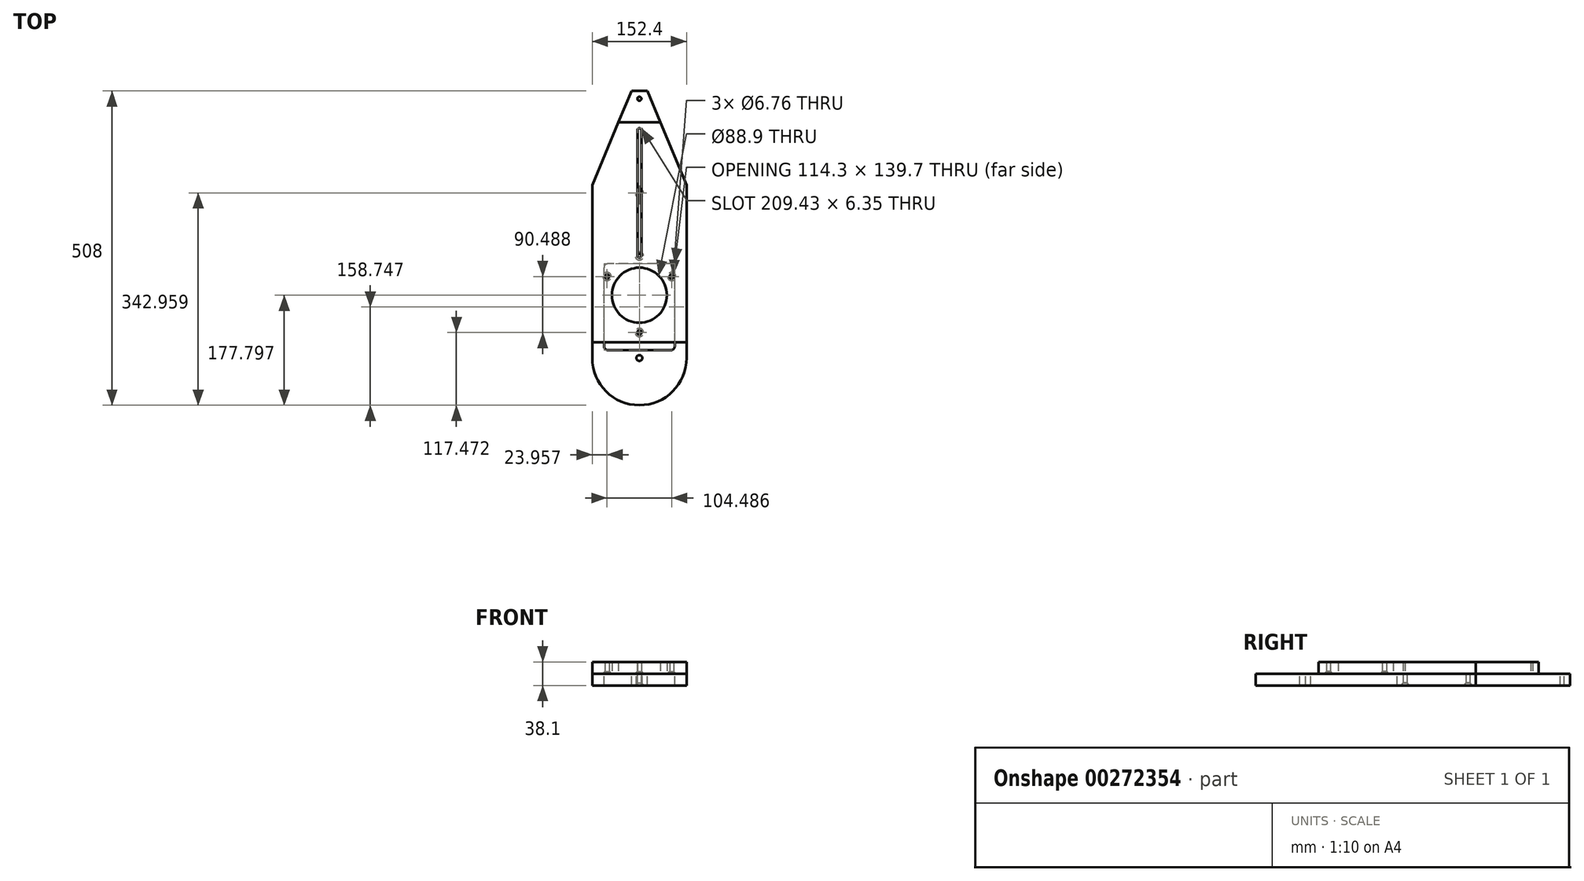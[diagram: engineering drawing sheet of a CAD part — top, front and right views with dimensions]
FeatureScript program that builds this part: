
annotation { "Feature Type Name" : "Feature", "Feature Type Description" : "" }
export const myFeature = defineFeature(function(context is Context, id is Id, definition is map)
    precondition{}
    {
        {
            var Q0;
            Q0=qCreatedBy(makeId("Top.planeOp"),FACE);
            var sketch = newSketch(context, id + "F0", { "sketchPlane" : qUnion([Q0])});
            skLineSegment(sketch, "E0.bottom", {"start": v(-112.58, 63.43) * mm, "end": v(-44.84, 63.43) * mm});
            skLineSegment(sketch, "E0.top", {"start": v(-154.9, -292.17) * mm, "end": v(-2.5, -292.17) * mm});
            skLineSegment(sketch, "E0.left", {"start": v(-154.9, -38.17) * mm, "end": v(-154.9, -292.17) * mm});
            skLineSegment(sketch, "E0.right", {"start": v(-2.5, -38.17) * mm, "end": v(-2.5, -292.17) * mm});
            skCircle(sketch, "E1", {"center": v(-78.7, -215.97) * mm, "radius": 44.45 * mm});
            skPoint(sketch, "E1.centerSnap0", {"position": v(-78.7, -292.17) * mm});
            skPoint(sketch, "E2", {"position": v(-78.7, -276.3) * mm});
            skLineSegment(sketch, "E3", {"start": v(-78.7, -215.97) * mm, "end": v(-0.55, -170.85) * mm, "construction": true});
            skLineSegment(sketch, "E4", {"start": v(-78.7, -215.97) * mm, "end": v(-157.21, -170.65) * mm, "construction": true});
            skCircle(sketch, "E5", {"center": v(-78.7, -215.97) * mm, "radius": 60.33 * mm, "construction": true});
            skPoint(sketch, "E6", {"position": v(-26.47, -185.81) * mm});
            skPoint(sketch, "E7", {"position": v(-130.95, -185.81) * mm});
            skLineSegment(sketch, "E8", {"start": v(-78.7, -165.17) * mm, "end": v(-78.7, 11.88) * mm, "construction": true});
            skLineSegment(sketch, "E9.left", {"start": v(-75.54, 50.85) * mm, "end": v(-75.53, -152.35) * mm});
            skLineSegment(sketch, "E9.right", {"start": v(-81.89, 50.73) * mm, "end": v(-81.88, -152.47) * mm});
            skPoint(sketch, "E9.middle", {"position": v(-78.7, -50.81) * mm});
            skArc(sketch, "E10", {"start": v(-81.89, 50.73) * mm, "mid": v(-78.77, 53.9) * mm, "end": v(-75.54, 50.85) * mm});
            skArc(sketch, "E11", {"start": v(-75.53, -152.35) * mm, "mid": v(-78.65, -155.52) * mm, "end": v(-81.88, -152.47) * mm});
            skCircle(sketch, "E12", {"center": v(-78.7, -317.57) * mm, "radius": 4.76 * mm});
            skLineSegment(sketch, "E13.bottom", {"start": v(-2.5, -292.17) * mm, "end": v(-154.9, -292.17) * mm});
            skLineSegment(sketch, "E13.left", {"start": v(-2.5, -292.17) * mm, "end": v(-2.5, -317.57) * mm});
            skLineSegment(sketch, "E13.right", {"start": v(-154.9, -292.17) * mm, "end": v(-154.9, -317.57) * mm});
            skLineSegment(sketch, "E14", {"start": v(-2.5, -38.17) * mm, "end": v(-66, 114.23) * mm});
            skLineSegment(sketch, "E15", {"start": v(-66, 114.23) * mm, "end": v(-78.7, 114.23) * mm});
            skLineSegment(sketch, "E16.MirrorCS", {"start": v(-154.9, -38.17) * mm, "end": v(-91.4, 114.23) * mm});
            skLineSegment(sketch, "E17.MirrorCS", {"start": v(-91.4, 114.23) * mm, "end": v(-78.7, 114.23) * mm});
            skCircle(sketch, "E18", {"center": v(-78.7, 101.53) * mm, "radius": 3.18 * mm});
            skLineSegment(sketch, "E19.bottom", {"start": v(-78.7, -304.87) * mm, "end": v(-27.9, -304.87) * mm});
            skLineSegment(sketch, "E19.top", {"start": v(-78.7, -165.17) * mm, "end": v(-27.9, -165.17) * mm});
            skLineSegment(sketch, "E19.right", {"start": v(-21.56, -298.52) * mm, "end": v(-21.56, -171.52) * mm});
            skLineSegment(sketch, "E20.trimOffspring", {"start": v(-78.7, -304.87) * mm, "end": v(-78.7, -314.95) * mm, "construction": true});
            skPoint(sketch, "E21.visualSharp", {"position": v(-21.56, -165.17) * mm});
            skArc(sketch, "E21.filletArc", {"start": v(-21.56, -171.52) * mm, "mid": v(-23.42, -167.03) * mm, "end": v(-27.9, -165.17) * mm});
            skPoint(sketch, "E22.visualSharp", {"position": v(-21.56, -304.87) * mm});
            skArc(sketch, "E22.filletArc", {"start": v(-27.9, -304.87) * mm, "mid": v(-23.42, -303.01) * mm, "end": v(-21.56, -298.52) * mm});
            skLineSegment(sketch, "E23.MirrorCS", {"start": v(-78.7, -165.17) * mm, "end": v(-129.5, -165.17) * mm});
            skArc(sketch, "E24.MirrorCS", {"start": v(-135.86, -171.52) * mm, "mid": v(-134, -167.03) * mm, "end": v(-129.5, -165.17) * mm});
            skLineSegment(sketch, "E25.MirrorCS", {"start": v(-135.86, -298.52) * mm, "end": v(-135.86, -171.52) * mm});
            skArc(sketch, "E26.MirrorCS", {"start": v(-129.5, -304.87) * mm, "mid": v(-134, -303.01) * mm, "end": v(-135.86, -298.52) * mm});
            skLineSegment(sketch, "E27.MirrorCS", {"start": v(-78.7, -304.87) * mm, "end": v(-129.5, -304.87) * mm});
            skArc(sketch, "E28", {"start": v(-81.88, -152.47) * mm, "mid": v(-78.65, -155.52) * mm, "end": v(-75.53, -152.35) * mm});
            skArc(sketch, "E29", {"start": v(-154.9, -317.57) * mm, "mid": v(-78.7, -393.77) * mm, "end": v(-2.5, -317.57) * mm});
            skPoint(sketch, "E30.center.orphan", {"position": v(-78.7, -50.87) * mm});
            skSolve(sketch);
        }
        {
            var Q0;
            {var subQ8=sQuery(id+"F0.wireOp",EDGE,"E0.bottom");Q0=makeQuery(id+"F0.imprint","IMPRINT",FACE,{"disambiguationData":[TD([[makeQuery(id+"F0.imprint","IMPRINT",EDGE,{"derivedFrom":subQ8}),-1.0]])]});}
            var Q1;
            Q1=makeQuery(id+"F0.imprint","IMPRINT",FACE,{"disambiguationData":[TD([[makeQuery(id+"F0.imprint","IMPRINT",EDGE,{"derivedFrom":sQuery(id+"F0.wireOp",EDGE,"E1")}),-1.0]])]});
            extrude(context, id + "F1", {"entities" : qUnion([Q0, Q1]), "depth" : 19.05 * mm});
        }
        {
            var Q0;
            Q0=sQuery(id+"F0.wireOp",VERTEX,"E6");
            var Q1;
            Q1=sQuery(id+"F0.wireOp",VERTEX,"E7");
            var Q2;
            Q2=sQuery(id+"F0.wireOp",VERTEX,"E2");
            var Q3;
            Q3=makeQuery(id+"F1.opExtrude","SWEPT_BODY",BODY,{"disambiguationData":[OSD([sQuery(id+"F0.wireOp",EDGE,"E0.bottom"),sQuery(id+"F0.wireOp",EDGE,"E0.top"),sQuery(id+"F0.wireOp",EDGE,"E0.left"),sQuery(id+"F0.wireOp",EDGE,"E0.right"),sQuery(id+"F0.wireOp",EDGE,"E1")])]});
            hole(context, id + "F2", {"style" : HoleStyle.C_SINK, "endStyle" : HoleEndStyle.THROUGH, "oppositeDirection" : true, "standardTappedOrClearance" : lookupTablePath({ "standard" : "ANSI", "fit" : "Normal (ASME)", "size" : "1/4", "type" : "Clearance" }), "standardBlindInLast" : lookupTablePath({ "fit" : "Free", "standard" : "ANSI", "size" : "1/4", "type" : "Clearance" }), "holeDiameter" : 6.76 * mm, "cSinkDiameter" : 13.5 * mm, "cSinkAngle" : 82 * degree, "isTappedThrough" : true, "tappedDepth" : 15.56 * mm, "tapClearance" : 3, "startFromSketch" : true, "locations" : qUnion([Q0, Q1, Q2]), "scope" : qUnion([Q3])});
        }
        {
            var Q0;
            Q0=makeQuery(id+"F0.imprint","IMPRINT",FACE,{"disambiguationData":[TD([[makeQuery(id+"F0.imprint","IMPRINT",EDGE,{"derivedFrom":sQuery(id+"F0.wireOp",EDGE,"E12")}),-1.0]])]});
            var Q1;
            {var subQ0=sQuery(id+"F0.wireOp",EDGE,"E0.bottom");Q1=makeQuery(id+"F0.imprint","IMPRINT",FACE,{"disambiguationData":[TD([[makeQuery(id+"F0.imprint","IMPRINT",EDGE,{"derivedFrom":subQ0}),-1.0]])]});}
            var Q2;
            {var subQ1=sQuery(id+"F0.wireOp",EDGE,"E0.bottom");Q2=makeQuery(id+"F0.imprint","IMPRINT",FACE,{"disambiguationData":[TD([[makeQuery(id+"F0.imprint","IMPRINT",EDGE,{"derivedFrom":subQ1}),1.0]])]});}
            var Q3;
            {var subQ0=sQuery(id+"F0.wireOp",EDGE,"E28");var subQ1=sQuery(id+"F0.wireOp",EDGE,"E9.left");var subQ2=makeQuery(id+"F0.imprint","INTERSECT",VERTEX,{"derivedFrom":[subQ1,subQ0]});Q3=makeQuery(id+"F0.imprint","IMPRINT",FACE,{"disambiguationData":[TD([[makeQuery(id+"F0.imprint","IMPRINT",EDGE,{"disambiguationData":[TD([[subQ2,1.0]])],"derivedFrom":subQ1}),-1.0]])]});}
            var Q4;
            {var subQ0=sQuery(id+"F0.wireOp",EDGE,"E10");Q4=makeQuery(id+"F0.imprint","IMPRINT",FACE,{"disambiguationData":[TD([[makeQuery(id+"F0.imprint","IMPRINT",EDGE,{"derivedFrom":subQ0}),-1.0]])]});}
            extrude(context, id + "F3", {"entities" : qUnion([Q0, Q1, Q2, Q3, Q4]), "oppositeDirection" : true, "depth" : 19.05 * mm});
        }
        {
            var Q0;
            Q0=makeQuery(id+"F3.opExtrude","CAP_FACE",FACE,{"disambiguationData":[OSD([sQuery(id+"F0.wireOp",EDGE,"E0.left"),sQuery(id+"F0.wireOp",EDGE,"E0.right"),sQuery(id+"F0.wireOp",EDGE,"E12"),sQuery(id+"F0.wireOp",EDGE,"E13.left"),sQuery(id+"F0.wireOp",EDGE,"E13.right"),sQuery(id+"F0.wireOp",EDGE,"E14"),sQuery(id+"F0.wireOp",EDGE,"E15"),sQuery(id+"F0.wireOp",EDGE,"E16.MirrorCS"),sQuery(id+"F0.wireOp",EDGE,"E17.MirrorCS"),sQuery(id+"F0.wireOp",EDGE,"E18"),sQuery(id+"F0.wireOp",EDGE,"E19.bottom"),sQuery(id+"F0.wireOp",EDGE,"E19.top"),sQuery(id+"F0.wireOp",EDGE,"E19.right"),sQuery(id+"F0.wireOp",EDGE,"E21.filletArc"),sQuery(id+"F0.wireOp",EDGE,"E22.filletArc"),sQuery(id+"F0.wireOp",EDGE,"E23.MirrorCS"),sQuery(id+"F0.wireOp",EDGE,"E24.MirrorCS"),sQuery(id+"F0.wireOp",EDGE,"E25.MirrorCS"),sQuery(id+"F0.wireOp",EDGE,"E26.MirrorCS"),sQuery(id+"F0.wireOp",EDGE,"E27.MirrorCS"),sQuery(id+"F0.wireOp",EDGE,"E29")])],"isStart":false});
            var sketch = newSketch(context, id + "F4", { "sketchPlane" : qUnion([Q0])});
            skLineSegment(sketch, "E31.0", {"start": v(-78.7, 165.17) * mm, "end": v(-78.7, -11.88) * mm, "construction": true});
            skPoint(sketch, "E32", {"position": v(-78.7, 152.47) * mm});
            skPoint(sketch, "E33", {"position": v(-78.7, 50.87) * mm});
            skSolve(sketch);
        }
        {
            var Q0;
            Q0=sQuery(id+"F4.wireOp",VERTEX,"E32");
            var Q1;
            Q1=sQuery(id+"F4.wireOp",VERTEX,"E33");
            var Q2;
            Q2=makeQuery(id+"F3.opExtrude","SWEPT_BODY",BODY,{"disambiguationData":[OSD([sQuery(id+"F0.wireOp",EDGE,"E0.left"),sQuery(id+"F0.wireOp",EDGE,"E0.right"),sQuery(id+"F0.wireOp",EDGE,"E12"),sQuery(id+"F0.wireOp",EDGE,"E13.left"),sQuery(id+"F0.wireOp",EDGE,"E13.right"),sQuery(id+"F0.wireOp",EDGE,"E14"),sQuery(id+"F0.wireOp",EDGE,"E15"),sQuery(id+"F0.wireOp",EDGE,"E16.MirrorCS"),sQuery(id+"F0.wireOp",EDGE,"E17.MirrorCS"),sQuery(id+"F0.wireOp",EDGE,"E18"),sQuery(id+"F0.wireOp",EDGE,"E19.bottom"),sQuery(id+"F0.wireOp",EDGE,"E19.top"),sQuery(id+"F0.wireOp",EDGE,"E19.right"),sQuery(id+"F0.wireOp",EDGE,"E21.filletArc"),sQuery(id+"F0.wireOp",EDGE,"E22.filletArc"),sQuery(id+"F0.wireOp",EDGE,"E23.MirrorCS"),sQuery(id+"F0.wireOp",EDGE,"E24.MirrorCS"),sQuery(id+"F0.wireOp",EDGE,"E25.MirrorCS"),sQuery(id+"F0.wireOp",EDGE,"E26.MirrorCS"),sQuery(id+"F0.wireOp",EDGE,"E27.MirrorCS"),sQuery(id+"F0.wireOp",EDGE,"E29")])]});
            hole(context, id + "F5", {"style" : HoleStyle.C_SINK, "endStyle" : HoleEndStyle.THROUGH, "standardTappedOrClearance" : lookupTablePath({ "standard" : "ANSI", "fit" : "Close", "size" : "1/4", "type" : "Clearance" }), "standardBlindInLast" : lookupTablePath({ "fit" : "Close", "standard" : "ANSI", "size" : "1/4", "type" : "Clearance" }), "holeDiameter" : 6.53 * mm, "cSinkDiameter" : 13.5 * mm, "cSinkAngle" : 82 * degree, "isTappedThrough" : true, "tappedDepth" : 15.57 * mm, "tapClearance" : 3, "locations" : qUnion([Q0, Q1]), "scope" : qUnion([Q2])});
        }
    });
